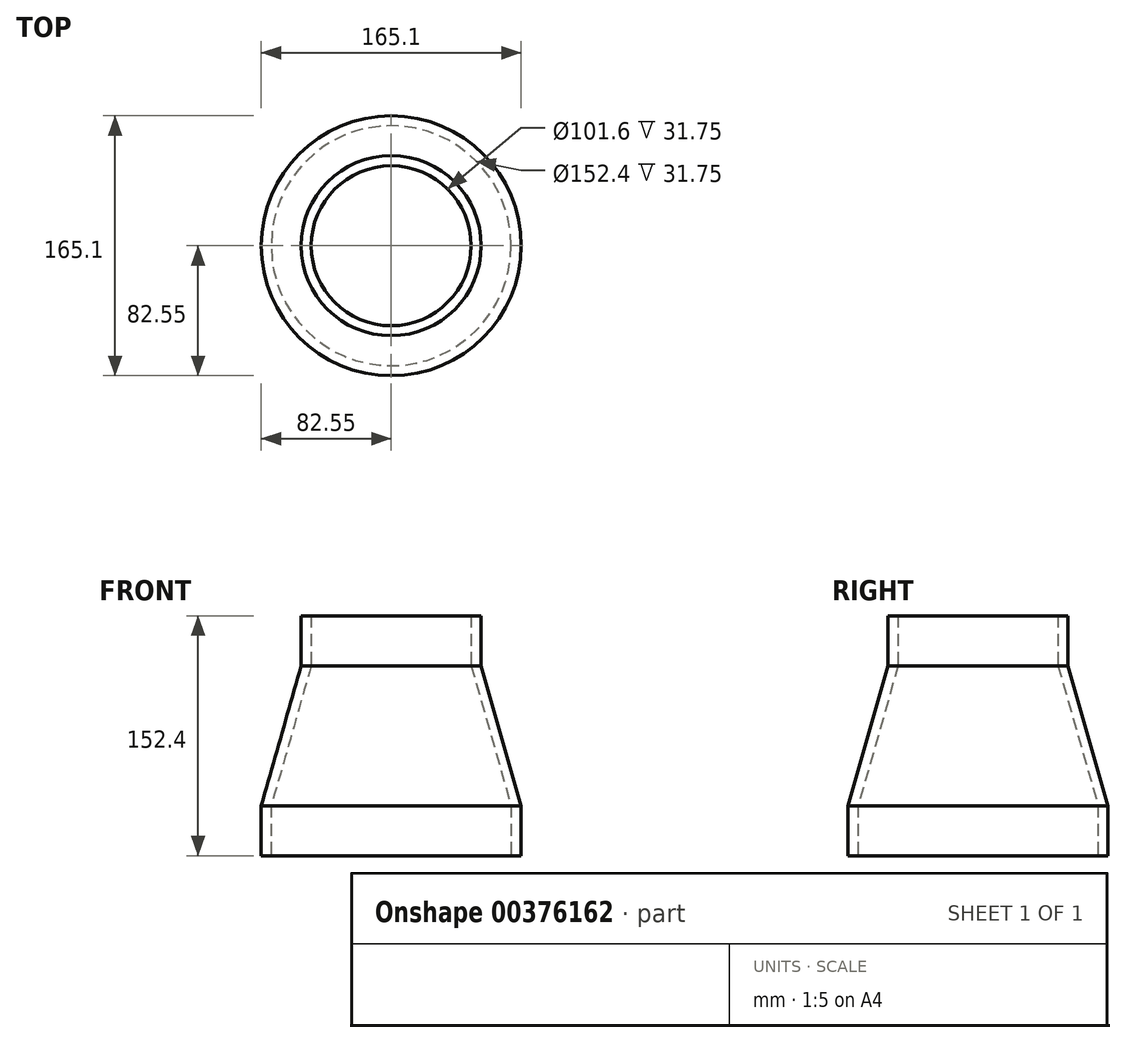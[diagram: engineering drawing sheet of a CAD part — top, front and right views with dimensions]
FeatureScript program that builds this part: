
annotation { "Feature Type Name" : "Feature", "Feature Type Description" : "" }
export const myFeature = defineFeature(function(context is Context, id is Id, definition is map)
    precondition{}
    {
        {
            var Q0;
            Q0=qCreatedBy(makeId("Front.planeOp"),FACE);
            var sketch = newSketch(context, id + "F0", { "sketchPlane" : qUnion([Q0])});
            skLineSegment(sketch, "E0", {"start": v(0, 0) * mm, "end": v(0, 152.4) * mm, "construction": true});
            skLineSegment(sketch, "E1", {"start": v(57.15, 152.4) * mm, "end": v(57.15, 120.65) * mm});
            skLineSegment(sketch, "E2", {"start": v(57.15, 120.65) * mm, "end": v(82.55, 31.75) * mm});
            skLineSegment(sketch, "E3", {"start": v(82.55, 31.75) * mm, "end": v(82.55, 0) * mm});
            skLineSegment(sketch, "E4", {"start": v(82.55, 0) * mm, "end": v(76.2, 0) * mm});
            skLineSegment(sketch, "E5", {"start": v(76.2, 0) * mm, "end": v(76.2, 31.75) * mm});
            skLineSegment(sketch, "E6", {"start": v(76.2, 31.75) * mm, "end": v(50.8, 120.65) * mm});
            skLineSegment(sketch, "E7", {"start": v(50.8, 120.65) * mm, "end": v(50.8, 152.4) * mm});
            skLineSegment(sketch, "E8", {"start": v(50.8, 152.4) * mm, "end": v(57.15, 152.4) * mm});
            skSolve(sketch);
        }
        {
            var Q0;
            Q0=makeQuery(id+"F0.imprint","IMPRINT",FACE,{"disambiguationData":[TD([[makeQuery(id+"F0.imprint","IMPRINT",EDGE,{"derivedFrom":sQuery(id+"F0.wireOp",EDGE,"E1")}),-1.0]])]});
            var Q1;
            Q1=sQuery(id+"F0.wireOp",EDGE,"E0");
            revolve(context, id + "F1", {"entities" : qUnion([Q0]), "axis" : qUnion([Q1]), "revolveType" : RevolveType.FULL});
        }
    });
